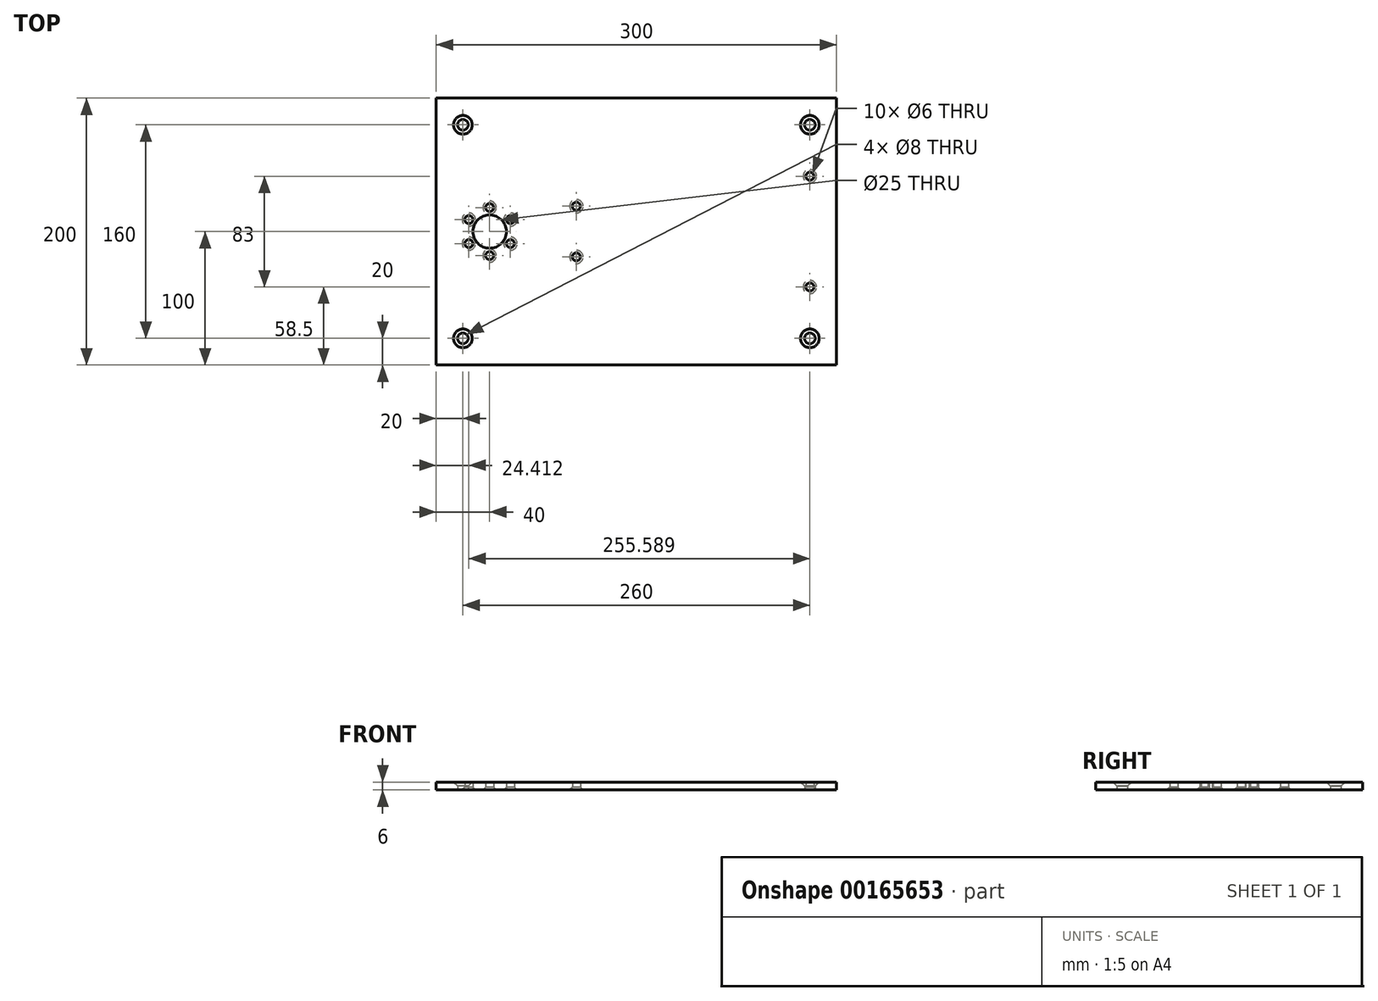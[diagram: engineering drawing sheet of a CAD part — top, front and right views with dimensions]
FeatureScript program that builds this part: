
annotation { "Feature Type Name" : "Feature", "Feature Type Description" : "" }
export const myFeature = defineFeature(function(context is Context, id is Id, definition is map)
    precondition{}
    {
        {
            var Q0;
            Q0=qCreatedBy(makeId("Top.planeOp"),FACE);
            var sketch = newSketch(context, id + "F0", { "sketchPlane" : qUnion([Q0])});
            skLineSegment(sketch, "E0.bottom", {"start": v(260, -100) * mm, "end": v(-40, -100) * mm});
            skLineSegment(sketch, "E0.top", {"start": v(260, 100) * mm, "end": v(-40, 100) * mm});
            skLineSegment(sketch, "E0.left", {"start": v(260, -100) * mm, "end": v(260, 100) * mm});
            skLineSegment(sketch, "E0.right", {"start": v(-40, -100) * mm, "end": v(-40, 100) * mm});
            skPoint(sketch, "E0.middle", {"position": v(110, 0) * mm});
            skCircle(sketch, "E1", {"center": v(0, 0) * mm, "radius": 12.5 * mm});
            skCircle(sketch, "E2", {"center": v(-20, 80) * mm, "radius": 4 * mm});
            skCircle(sketch, "E3", {"center": v(240, 80) * mm, "radius": 4 * mm});
            skCircle(sketch, "E4.MirrorC", {"center": v(-20, -80) * mm, "radius": 4 * mm});
            skCircle(sketch, "E5.MirrorC", {"center": v(240, -80) * mm, "radius": 4 * mm});
            skCircle(sketch, "E6", {"center": v(65, 19) * mm, "radius": 3 * mm});
            skCircle(sketch, "E7", {"center": v(240, 41.5) * mm, "radius": 3 * mm});
            skCircle(sketch, "E8.MirrorC", {"center": v(65, -19) * mm, "radius": 3 * mm});
            skCircle(sketch, "E9.MirrorC", {"center": v(240, -41.5) * mm, "radius": 3 * mm});
            skCircle(sketch, "E10", {"center": v(0, 18) * mm, "radius": 3 * mm});
            skCircle(sketch, "E11.1.0", {"center": v(-15.59, 9) * mm, "radius": 3 * mm});
            skCircle(sketch, "E11.2.0", {"center": v(-15.59, -9) * mm, "radius": 3 * mm});
            skCircle(sketch, "E11.3.0", {"center": v(0, -18) * mm, "radius": 3 * mm});
            skCircle(sketch, "E11.4.0", {"center": v(15.59, -9) * mm, "radius": 3 * mm});
            skCircle(sketch, "E11.5.0", {"center": v(15.59, 9) * mm, "radius": 3 * mm});
            skSolve(sketch);
        }
        {
            var Q0;
            Q0=makeQuery(id+"F0.imprint","IMPRINT",FACE,{"disambiguationData":[TD([[makeQuery(id+"F0.imprint","IMPRINT",EDGE,{"derivedFrom":sQuery(id+"F0.wireOp",EDGE,"E0.bottom")}),-1.0]])]});
            extrude(context, id + "F1", {"entities" : qUnion([Q0]), "depth" : 6 * mm, "offsetDistance" : 25 * mm});
        }
        {
            var Q0;
            Q0=makeQuery(id+"F1.opExtrude","CAP_EDGE",EDGE,{"disambiguationData":[OSD([sQuery(id+"F0.wireOp",EDGE,"E2")])],"isStart":false});
            var Q1;
            Q1=makeQuery(id+"F1.opExtrude","CAP_EDGE",EDGE,{"disambiguationData":[OSD([sQuery(id+"F0.wireOp",EDGE,"E3")])],"isStart":false});
            var Q2;
            Q2=makeQuery(id+"F1.opExtrude","CAP_EDGE",EDGE,{"disambiguationData":[OSD([sQuery(id+"F0.wireOp",EDGE,"E5.MirrorC")])],"isStart":false});
            var Q3;
            Q3=makeQuery(id+"F1.opExtrude","CAP_EDGE",EDGE,{"disambiguationData":[OSD([sQuery(id+"F0.wireOp",EDGE,"E4.MirrorC")])],"isStart":false});
            chamfer(context, id + "F2", {"entities" : qUnion([Q0, Q1, Q2, Q3]), "width" : 3 * mm, "tangentPropagation" : true});
        }
        {
            var Q0;
            Q0=makeQuery(id+"F1.opExtrude","CAP_EDGE",EDGE,{"disambiguationData":[OSD([sQuery(id+"F0.wireOp",EDGE,"E8.MirrorC")])],"isStart":true});
            var Q1;
            Q1=makeQuery(id+"F1.opExtrude","CAP_EDGE",EDGE,{"disambiguationData":[OSD([sQuery(id+"F0.wireOp",EDGE,"E9.MirrorC")])],"isStart":true});
            var Q2;
            Q2=makeQuery(id+"F1.opExtrude","CAP_EDGE",EDGE,{"disambiguationData":[OSD([sQuery(id+"F0.wireOp",EDGE,"E7")])],"isStart":true});
            var Q3;
            Q3=makeQuery(id+"F1.opExtrude","CAP_EDGE",EDGE,{"disambiguationData":[OSD([sQuery(id+"F0.wireOp",EDGE,"E6")])],"isStart":true});
            var Q4;
            Q4=makeQuery(id+"F1.opExtrude","CAP_EDGE",EDGE,{"disambiguationData":[OSD([sQuery(id+"F0.wireOp",EDGE,"E11.3.0")])],"isStart":true});
            var Q5;
            Q5=makeQuery(id+"F1.opExtrude","CAP_EDGE",EDGE,{"disambiguationData":[OSD([sQuery(id+"F0.wireOp",EDGE,"E11.2.0")])],"isStart":true});
            var Q6;
            Q6=makeQuery(id+"F1.opExtrude","CAP_EDGE",EDGE,{"disambiguationData":[OSD([sQuery(id+"F0.wireOp",EDGE,"E11.1.0")])],"isStart":true});
            var Q7;
            Q7=makeQuery(id+"F1.opExtrude","CAP_EDGE",EDGE,{"disambiguationData":[OSD([sQuery(id+"F0.wireOp",EDGE,"E11.4.0")])],"isStart":true});
            var Q8;
            Q8=makeQuery(id+"F1.opExtrude","CAP_EDGE",EDGE,{"disambiguationData":[OSD([sQuery(id+"F0.wireOp",EDGE,"E11.5.0")])],"isStart":true});
            var Q9;
            Q9=makeQuery(id+"F1.opExtrude","CAP_EDGE",EDGE,{"disambiguationData":[OSD([sQuery(id+"F0.wireOp",EDGE,"E10")])],"isStart":true});
            chamfer(context, id + "F3", {"entities" : qUnion([Q0, Q1, Q2, Q3, Q4, Q5, Q6, Q7, Q8, Q9]), "width" : 2 * mm, "tangentPropagation" : true});
        }
    });
